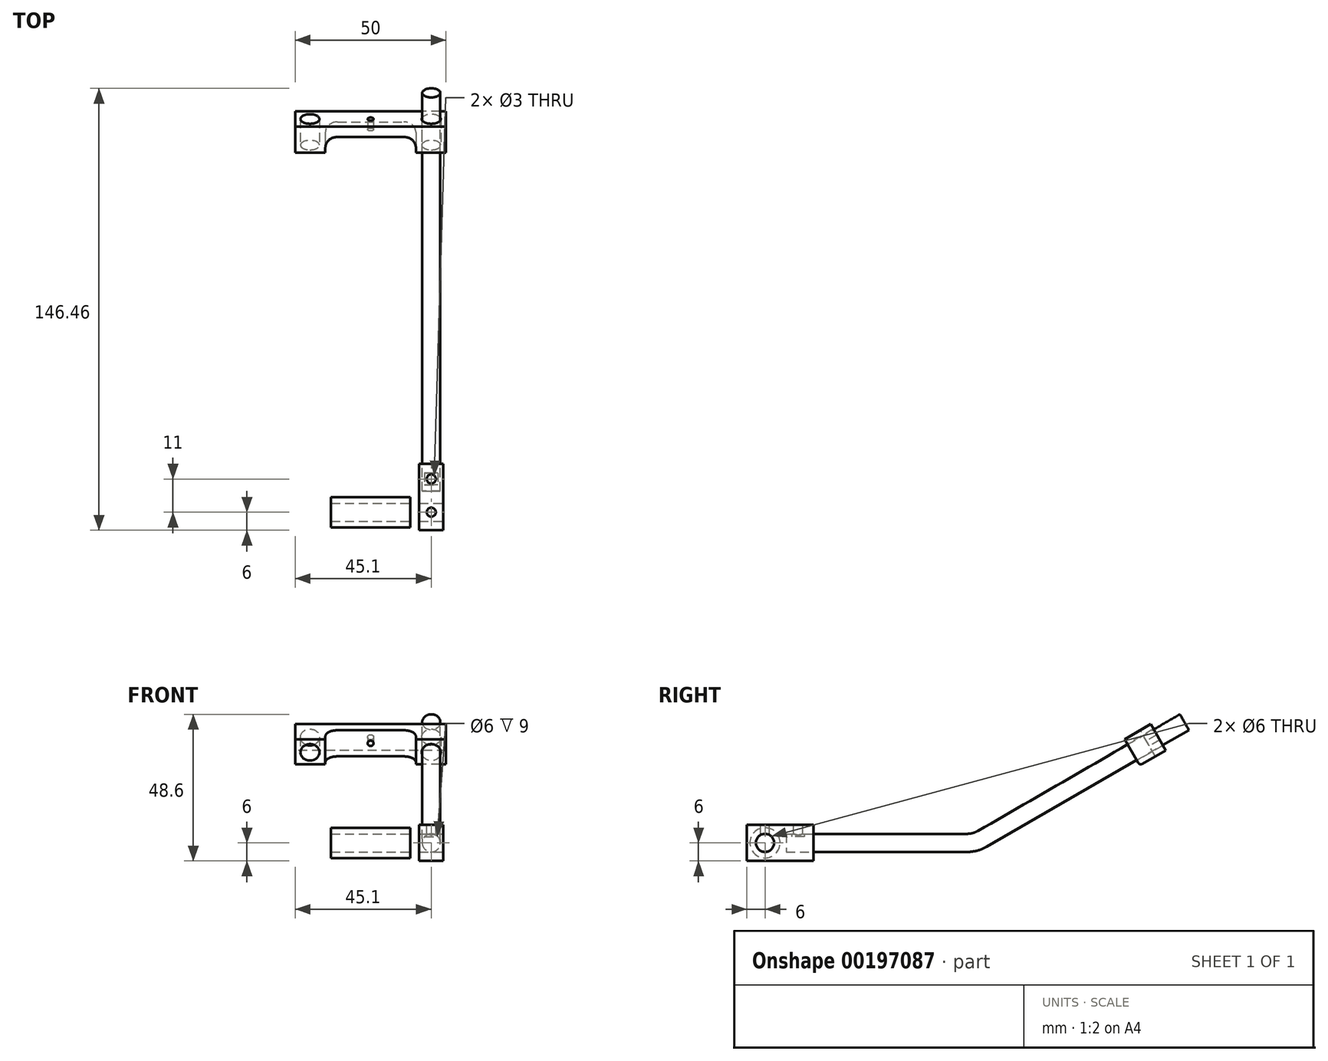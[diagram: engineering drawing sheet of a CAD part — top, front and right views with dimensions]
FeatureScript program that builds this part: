
annotation { "Feature Type Name" : "Feature", "Feature Type Description" : "" }
export const myFeature = defineFeature(function(context is Context, id is Id, definition is map)
    precondition{}
    {
        {
            var Q0;
            Q0=qCreatedBy(makeId("Right.planeOp"),FACE);
            var sketch = newSketch(context, id + "F0", { "sketchPlane" : qUnion([Q0])});
            skCircle(sketch, "E0.0", {"center": v(0, 0) * mm, "radius": 5 * mm});
            skSolve(sketch);
        }
        {
            var Q0;
            Q0=qSketchRegion(id+"F0",true);
            extrude(context, id + "F1", {"entities" : qUnion([Q0]), "endBound" : BoundingType.SYMMETRIC, "depth" : 48.2 * mm});
        }
        {
            var Q0;
            Q0=makeQuery(id+"F1.opExtrude","CAP_FACE",FACE,{"disambiguationData":[OSD([sQuery(id+"F0.wireOp",EDGE,"E0.0")])],"isStart":false});
            var sketch = newSketch(context, id + "F2", { "sketchPlane" : qUnion([Q0])});
            skCircle(sketch, "E1.0", {"center": v(0, 0) * mm, "radius": 3 * mm});
            skCircle(sketch, "E2.0", {"center": v(0, 0) * mm, "radius": 5 * mm});
            skSolve(sketch);
        }
        {
            var Q0;
            Q0 = qSketchRegion(id + "F2", true);
            extrude(context, id + "F3", {"entities" : qUnion([Q0]), "operationType" : NewBodyOperationType.REMOVE, "oppositeDirection" : true, "depth" : 11 * mm});
        }
        {
            var Q0;
            Q0=makeQuery(id+"F1.opExtrude","CAP_FACE",FACE,{"disambiguationData":[OSD([sQuery(id+"F0.wireOp",EDGE,"E0.0")])],"isStart":true});
            var sketch = newSketch(context, id + "F4", { "sketchPlane" : qUnion([Q0])});
            skCircle(sketch, "E3.0", {"center": v(0, 0) * mm, "radius": 3 * mm});
            skCircle(sketch, "E4.0", {"center": v(0, 0) * mm, "radius": 5 * mm});
            skSolve(sketch);
        }
        {
            var Q0;
            Q0 = qSketchRegion(id + "F4", true);
            extrude(context, id + "F5", {"entities" : qUnion([Q0]), "operationType" : NewBodyOperationType.REMOVE, "oppositeDirection" : true, "depth" : 11 * mm});
        }
        {
            var Q0;
            Q0=makeQuery(id+"F1.opExtrude","CAP_FACE",FACE,{"disambiguationData":[OSD([sQuery(id+"F0.wireOp",EDGE,"E0.0")])],"isStart":false});
            var sketch = newSketch(context, id + "F6", { "sketchPlane" : qUnion([Q0])});
            skArc(sketch, "E5", {"start": v(-2.24, 2) * mm, "mid": v(0, 3) * mm, "end": v(2.24, 2) * mm});
            skLineSegment(sketch, "E6", {"start": v(-2.24, 2) * mm, "end": v(2.24, 2) * mm});
            skSolve(sketch);
        }
        {
            var Q0;
            Q0=qSketchRegion(id+"F6",true);
            extrude(context, id + "F7", {"entities" : qUnion([Q0]), "operationType" : NewBodyOperationType.REMOVE, "oppositeDirection" : true, "depth" : 6 * mm});
        }
        {
            var Q0;
            Q0=makeQuery(id+"F1.opExtrude","CAP_FACE",FACE,{"disambiguationData":[OSD([sQuery(id+"F0.wireOp",EDGE,"E0.0")])],"isStart":true});
            var sketch = newSketch(context, id + "F8", { "sketchPlane" : qUnion([Q0])});
            skArc(sketch, "E7.0", {"start": v(2.24, 2) * mm, "mid": v(0, 3) * mm, "end": v(-2.24, 2) * mm});
            skLineSegment(sketch, "E7.1", {"start": v(2.24, 2) * mm, "end": v(-2.24, 2) * mm});
            skSolve(sketch);
        }
        {
            var Q0;
            Q0=qSketchRegion(id+"F8",true);
            extrude(context, id + "F9", {"entities" : qUnion([Q0]), "operationType" : NewBodyOperationType.REMOVE, "oppositeDirection" : true, "depth" : 6 * mm});
        }
        {
            var Q0;
            Q0=makeQuery(id+"F1.opExtrude","CAP_FACE",FACE,{"disambiguationData":[OSD([sQuery(id+"F0.wireOp",EDGE,"E0.0")])],"isStart":false});
            var sketch = newSketch(context, id + "F10", { "sketchPlane" : qUnion([Q0])});
            skLineSegment(sketch, "E8.bottom", {"start": v(-6, 6) * mm, "end": v(16, 6) * mm});
            skLineSegment(sketch, "E8.top", {"start": v(-6, -6) * mm, "end": v(16, -6) * mm});
            skLineSegment(sketch, "E8.left", {"start": v(-6, 6) * mm, "end": v(-6, -6) * mm});
            skLineSegment(sketch, "E8.right", {"start": v(16, 6) * mm, "end": v(16, -6) * mm});
            skPoint(sketch, "E9", {"position": v(-6, 0) * mm});
            skSolve(sketch);
        }
        {
            var Q0;
            Q0=qSketchRegion(id+"F10",true);
            extrude(context, id + "F11", {"entities" : qUnion([Q0]), "oppositeDirection" : true, "depth" : 8 * mm});
        }
        {
            var Q0;
            Q0=makeQuery(id+"F11.opExtrude","CAP_FACE",FACE,{"disambiguationData":[OSD([sQuery(id+"F10.wireOp",EDGE,"E8.bottom"),sQuery(id+"F10.wireOp",EDGE,"E8.top"),sQuery(id+"F10.wireOp",EDGE,"E8.left"),sQuery(id+"F10.wireOp",EDGE,"E8.right")])],"isStart":true});
            var sketch = newSketch(context, id + "F12", { "sketchPlane" : qUnion([Q0])});
            skCircle(sketch, "E10.0", {"center": v(0, 0) * mm, "radius": 3 * mm});
            skSolve(sketch);
        }
        {
            var Q0;
            Q0=qSketchRegion(id+"F12",true);
            extrude(context, id + "F13", {"entities" : qUnion([Q0]), "operationType" : NewBodyOperationType.REMOVE, "endBound" : BoundingType.THROUGH_ALL, "oppositeDirection" : true, "depth" : 25 * mm});
        }
        {
            var Q0;
            Q0=makeQuery(id+"F11.opExtrude","SWEPT_FACE",FACE,{"disambiguationData":[OSD([sQuery(id+"F10.wireOp",EDGE,"E8.right")])]});
            var sketch = newSketch(context, id + "F14", { "sketchPlane" : qUnion([Q0])});
            skCircle(sketch, "E11", {"center": v(-20.1, 0) * mm, "radius": 3 * mm});
            skLineSegment(sketch, "E12", {"start": v(-24.1, -6) * mm, "end": v(-16.1, 6) * mm, "construction": true});
            skSolve(sketch);
        }
        {
            var Q0;
            Q0=qSketchRegion(id+"F14",true);
            extrude(context, id + "F15", {"entities" : qUnion([Q0]), "operationType" : NewBodyOperationType.REMOVE, "oppositeDirection" : true, "depth" : 9 * mm});
        }
        {
            var Q0;
            Q0=makeQuery(id+"F11.opExtrude","SWEPT_FACE",FACE,{"disambiguationData":[OSD([sQuery(id+"F10.wireOp",EDGE,"E8.bottom")])]});
            var sketch = newSketch(context, id + "F16", { "sketchPlane" : qUnion([Q0])});
            skCircle(sketch, "E13", {"center": v(20.1, 0) * mm, "radius": 1.5 * mm});
            skLineSegment(sketch, "E14", {"start": v(20.1, 0) * mm, "end": v(20.1, -6) * mm, "construction": true});
            skSolve(sketch);
        }
        {
            var Q0;
            Q0=qSketchRegion(id+"F16",true);
            var Q1;
            Q1=makeQuery(id+"F13.boolean.opBoolean","COPY",FACE,{"derivedFrom":makeQuery(id+"F13.opExtrude","SWEPT_FACE",FACE,{"disambiguationData":[OSD([sQuery(id+"F12.wireOp",EDGE,"E10.0")])]})});
            extrude(context, id + "F17", {"entities" : qUnion([Q0]), "operationType" : NewBodyOperationType.REMOVE, "endBound" : BoundingType.UP_TO_SURFACE, "oppositeDirection" : true, "endBoundEntityFace" : qUnion([Q1]), "depth" : 25 * mm});
        }
        {
            var Q0;
            Q0=makeQuery(id+"F11.opExtrude","SWEPT_FACE",FACE,{"disambiguationData":[OSD([sQuery(id+"F10.wireOp",EDGE,"E8.bottom")])]});
            var sketch = newSketch(context, id + "F18", { "sketchPlane" : qUnion([Q0])});
            skCircle(sketch, "E15", {"center": v(20.1, 11) * mm, "radius": 1.5 * mm});
            skSolve(sketch);
        }
        {
            var Q0;
            Q0=qSketchRegion(id+"F18",true);
            var Q1;
            Q1=makeQuery(id+"F15.boolean.opBoolean","COPY",FACE,{"derivedFrom":makeQuery(id+"F15.opExtrude","SWEPT_FACE",FACE,{"disambiguationData":[OSD([sQuery(id+"F14.wireOp",EDGE,"E11")])]})});
            extrude(context, id + "F19", {"entities" : qUnion([Q0]), "operationType" : NewBodyOperationType.REMOVE, "endBound" : BoundingType.UP_TO_SURFACE, "oppositeDirection" : true, "endBoundEntityFace" : qUnion([Q1]), "depth" : 25 * mm});
        }
        {
            var Q0;
            Q0=makeQuery(id+"F15.boolean.opBoolean","COPY",FACE,{"derivedFrom":makeQuery(id+"F15.opExtrude","CAP_FACE",FACE,{"disambiguationData":[OSD([sQuery(id+"F14.wireOp",EDGE,"E11")])],"isStart":false})});
            var sketch = newSketch(context, id + "F20", { "sketchPlane" : qUnion([Q0])});
            skCircle(sketch, "E16.0", {"center": v(-20.1, 0) * mm, "radius": 3 * mm});
            skSolve(sketch);
        }
        {
            var Q0;
            Q0=qCreatedBy(makeId("Right.planeOp"),FACE);
            var sketch = newSketch(context, id + "F21", { "sketchPlane" : qUnion([Q0])});
            skLineSegment(sketch, "E17", {"start": v(7, 0) * mm, "end": v(67, 0) * mm});
            skLineSegment(sketch, "E18", {"start": v(72, 1.34) * mm, "end": v(138.96, 40) * mm});
            skPoint(sketch, "E19.visualSharp", {"position": v(69.68, 0) * mm});
            skArc(sketch, "E19.filletArc", {"start": v(67, 0) * mm, "mid": v(69.59, 0.34) * mm, "end": v(72, 1.34) * mm});
            skSolve(sketch);
        }
        {
            var Q0;
            Q0=qSketchRegion(id+"F20",true);
            var Q1;
            Q1=qConstructionFilter(qBodyType(qCreatedBy(id+"F21",EDGE),BodyType.WIRE),ConstructionObject.NO);
            sweep(context, id + "F22", {"profiles" : qUnion([Q0]), "path" : qUnion([Q1])});
        }
        {
            var Q0;
            Q0=makeQuery(id+"F22.opSweep","CAP_FACE",FACE,{"disambiguationData":[OSD([sQuery(id+"F20.wireOp",EDGE,"E16.0"),sQuery(id+"F21.wireOp",VERTEX,"E17.start")])],"isStart":true});
            cPlane(context, id + "F23", {"entities" : qUnion([Q0]), "cplaneType" : CPlaneType.OFFSET, "offset" : 2 * mm, "oppositeDirection" : true, "width" : 150 * mm, "height" : 150 * mm});
        }
        {
            var Q0;
            Q0=qCreatedBy(id+"F23.planeOp",FACE);
            var sketch = newSketch(context, id + "F24", { "sketchPlane" : qUnion([Q0])});
            skArc(sketch, "E20", {"start": v(22.34, 2) * mm, "mid": v(20.1, 3) * mm, "end": v(17.86, 2) * mm});
            skLineSegment(sketch, "E21", {"start": v(22.34, 2) * mm, "end": v(22.34, 2) * mm});
            skLineSegment(sketch, "E22", {"start": v(17.86, 2) * mm, "end": v(22.34, 2) * mm});
            skSolve(sketch);
        }
        {
            var Q0;
            Q0=qSketchRegion(id+"F24",true);
            extrude(context, id + "F25", {"entities" : qUnion([Q0]), "operationType" : NewBodyOperationType.REMOVE, "oppositeDirection" : true, "depth" : 4 * mm});
        }
        {
            var Q0;
            Q0=makeQuery(id+"F22.opSweep","CAP_FACE",FACE,{"disambiguationData":[OSD([sQuery(id+"F20.wireOp",EDGE,"E16.0"),sQuery(id+"F21.wireOp",VERTEX,"E18.end")])],"isStart":false});
            cPlane(context, id + "F26", {"entities" : qUnion([Q0]), "cplaneType" : CPlaneType.OFFSET, "offset" : 20 * mm, "oppositeDirection" : true, "width" : 150 * mm, "height" : 150 * mm});
        }
        {
            var Q0;
            Q0=qCreatedBy(id+"F26.planeOp",FACE);
            var sketch = newSketch(context, id + "F27", { "sketchPlane" : qUnion([Q0])});
            skLineSegment(sketch, "E23.bottom", {"start": v(-25, -29.84) * mm, "end": v(25, -29.84) * mm});
            skLineSegment(sketch, "E23.top", {"start": v(-25, -39.84) * mm, "end": v(25, -39.84) * mm});
            skLineSegment(sketch, "E23.left", {"start": v(-25, -29.84) * mm, "end": v(-25, -39.84) * mm});
            skLineSegment(sketch, "E23.right", {"start": v(25, -29.84) * mm, "end": v(25, -39.84) * mm});
            skPoint(sketch, "E23.middle", {"position": v(0, -34.84) * mm});
            skPoint(sketch, "E24", {"position": v(-20.1, -34.84) * mm});
            skCircle(sketch, "E25", {"center": v(-20.1, -34.84) * mm, "radius": 3.15 * mm});
            skLineSegment(sketch, "E26", {"start": v(0, -31.94) * mm, "end": v(0, -38.42) * mm, "construction": true});
            skCircle(sketch, "E27.MirrorC", {"center": v(20.1, -34.84) * mm, "radius": 3.15 * mm});
            skCircle(sketch, "E28", {"center": v(0, -34.84) * mm, "radius": 1 * mm});
            skSolve(sketch);
        }
        {
            var Q0;
            Q0 = qSketchRegion(id + "F27", true);
            extrude(context, id + "F28", {"entities" : qUnion([Q0]), "depth" : 10 * mm});
        }
        {
            var Q0;
            Q0=makeQuery(id+"F28.opExtrude","SWEPT_FACE",FACE,{"disambiguationData":[OSD([sQuery(id+"F27.wireOp",EDGE,"E23.bottom")])]});
            var sketch = newSketch(context, id + "F29", { "sketchPlane" : qUnion([Q0])});
            skLineSegment(sketch, "E29.bottom", {"start": v(-15, 126.34) * mm, "end": v(15, 126.34) * mm});
            skLineSegment(sketch, "E29.top", {"start": v(-15, 120.34) * mm, "end": v(15, 120.34) * mm});
            skLineSegment(sketch, "E29.left", {"start": v(-15, 126.34) * mm, "end": v(-15, 120.34) * mm});
            skLineSegment(sketch, "E29.right", {"start": v(15, 126.34) * mm, "end": v(15, 120.34) * mm});
            skSolve(sketch);
        }
        {
            var Q0;
            Q0 = qSketchRegion(id + "F29", true);
            extrude(context, id + "F30", {"entities" : qUnion([Q0]), "operationType" : NewBodyOperationType.REMOVE, "endBound" : BoundingType.THROUGH_ALL, "oppositeDirection" : true, "depth" : 25 * mm});
        }
        {
            var Q0;
            Q0=makeQuery(id+"F30.boolean.opBoolean","COPY",EDGE,{"derivedFrom":makeQuery(id+"F30.opExtrude","SWEPT_EDGE",EDGE,{"disambiguationData":[OSD([sQuery(id+"F29.wireOp",EDGE,"E29.bottom"),sQuery(id+"F29.wireOp",EDGE,"E29.left")])]})});
            var Q1;
            Q1=makeQuery(id+"F30.boolean.opBoolean","COPY",EDGE,{"derivedFrom":makeQuery(id+"F30.opExtrude","SWEPT_EDGE",EDGE,{"disambiguationData":[OSD([sQuery(id+"F29.wireOp",EDGE,"E29.bottom"),sQuery(id+"F29.wireOp",EDGE,"E29.right")])]})});
            fillet(context, id + "F31", {"entities" : qUnion([Q0, Q1]), "radius" : 4 * mm, "tangentPropagation" : true, "allowEdgeOverflow" : false});
        }
        {
            var Q0;
            {var subQ0=sQuery(id+"F27.wireOp",EDGE,"E23.left");var subQ1=sQuery(id+"F27.wireOp",EDGE,"E23.top");Q0=makeQuery(id+"F30.boolean.opBoolean","SPLIT",EDGE,{"disambiguationData":[TD([makeQuery(id+"F28.opExtrude","SWEPT_FACE",FACE,{"disambiguationData":[OSD([subQ0])]})])],"derivedFrom":makeQuery(id+"F28.opExtrude","CAP_EDGE",EDGE,{"disambiguationData":[OSD([subQ1])],"isStart":true})});}
            var Q1;
            {var subQ0=sQuery(id+"F27.wireOp",EDGE,"E23.right");var subQ1=sQuery(id+"F27.wireOp",EDGE,"E23.top");Q1=makeQuery(id+"F30.boolean.opBoolean","SPLIT",EDGE,{"disambiguationData":[TD([makeQuery(id+"F28.opExtrude","SWEPT_FACE",FACE,{"disambiguationData":[OSD([subQ0])]})])],"derivedFrom":makeQuery(id+"F28.opExtrude","CAP_EDGE",EDGE,{"disambiguationData":[OSD([subQ1])],"isStart":true})});}
            fillet(context, id + "F32", {"entities" : qUnion([Q0, Q1]), "radius" : 1 * mm, "tangentPropagation" : true, "allowEdgeOverflow" : false});
        }
    });
